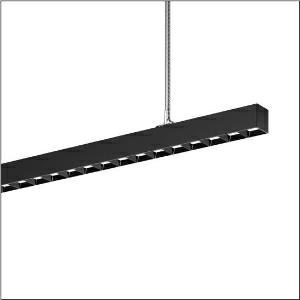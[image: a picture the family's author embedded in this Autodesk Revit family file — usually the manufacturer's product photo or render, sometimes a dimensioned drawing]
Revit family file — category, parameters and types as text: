
# Revit family: silica_r__21_51mx31dc3dbb_16a7
name_source: partatom
category: Lighting Fixtures
units: mm (PartAtom-declared; Revit-internal decimal feet)

## family parameters
Cut with Voids When Loaded = No
Host = Face
Light Source = No
Part Type = Normal
Room Calculation Point = No
Round Connector Dimension = Use Diameter
Shared = No

## types (1)
- --- (1 x LED, 18230 lm, 113.3 W, 3000K)
    Apparent Load = 113 VA
    CIE Flux Codes = 87 99 100 59 100
    Color Rendering = 80
    Color Temperature = 3000K
    Default Elevation = 1800 mm
    Description = Silica® 21, office luminaire, primary light control with darklight reflector, of PMMA, black, CAT 2 (L<= 3000cd/m²), light emission: direct/indirect distribution, primary light characteristic: symmetric, installation type: suspended mounting, LED, rated luminous flux: 18.230lm, luminous efficacy: 161lm/W, light colour: 830, colour temperature: 3000K, with terminal, 3+2-pole, max. 2.5mm², mains connection: 220..240V, AC, 50/60Hz, rated input power: 113.3W, luminaire housing, of aluminium, jet black (RAL 9005), length: 3.004mm, width: 53mm, height: 53mm, protection rating (complete): IP20, insulation class (complete): insulation class I (protective earthing), certification: CE, permissible operating ambient temperature: 0..+35°C, standard: EN 50419, packaging unit: 1 piece
    Height = 53 mm
    Lamp = 1 x LED
    Lamp Light Flux = 18230 lm
    Lamp Power = 113.3 W
    Lamp count = 1
    Length = 3004 mm
    Luminous efficacy = 161 lm/W
    Manufacturer = Siteco
    ModVariant = No
    Model = 51MX31DC3DBB
    Mounting Place = Ceiling
    Mounting Type = Pendant
    Number of Poles = 1
    OnlyDefault = Yes
    Power Factor = 1
    Product Name = Silica® 21
    Product group = office luminaire | ceiling pendant
    ProductGroupID = 902
    Protection Class = Protection class I
    Protection Degree = IP 20
    RLX_Detail_Level = 1
    RLX_Emergency_Light_Flux = 0 lm
    RLX_Emergency_Type = 0
    RLX_Emergency_Type_DB = No
    RlxData = <blob elided: 66837 chars, md5=2c19fc12>
    Socket = socket
    Standby Power = 0 W
    System Light Flux = 18230 lm
    System Power = 113 W
    Type Comments = factory setting: luminous flux: 100 % | dim-lin: 254 | 392 mA
    Type Image = l_1335852.jpg
    URL = http://relux.com
    VarID = @adj_090563
    Voltage = 0 V
    Weight = 0.00 kg
    Width = 53 mm

## geometry (parser evidence)
native form markers: Blend x4, Sweep x11
no freeform markers — native parametric forms only
